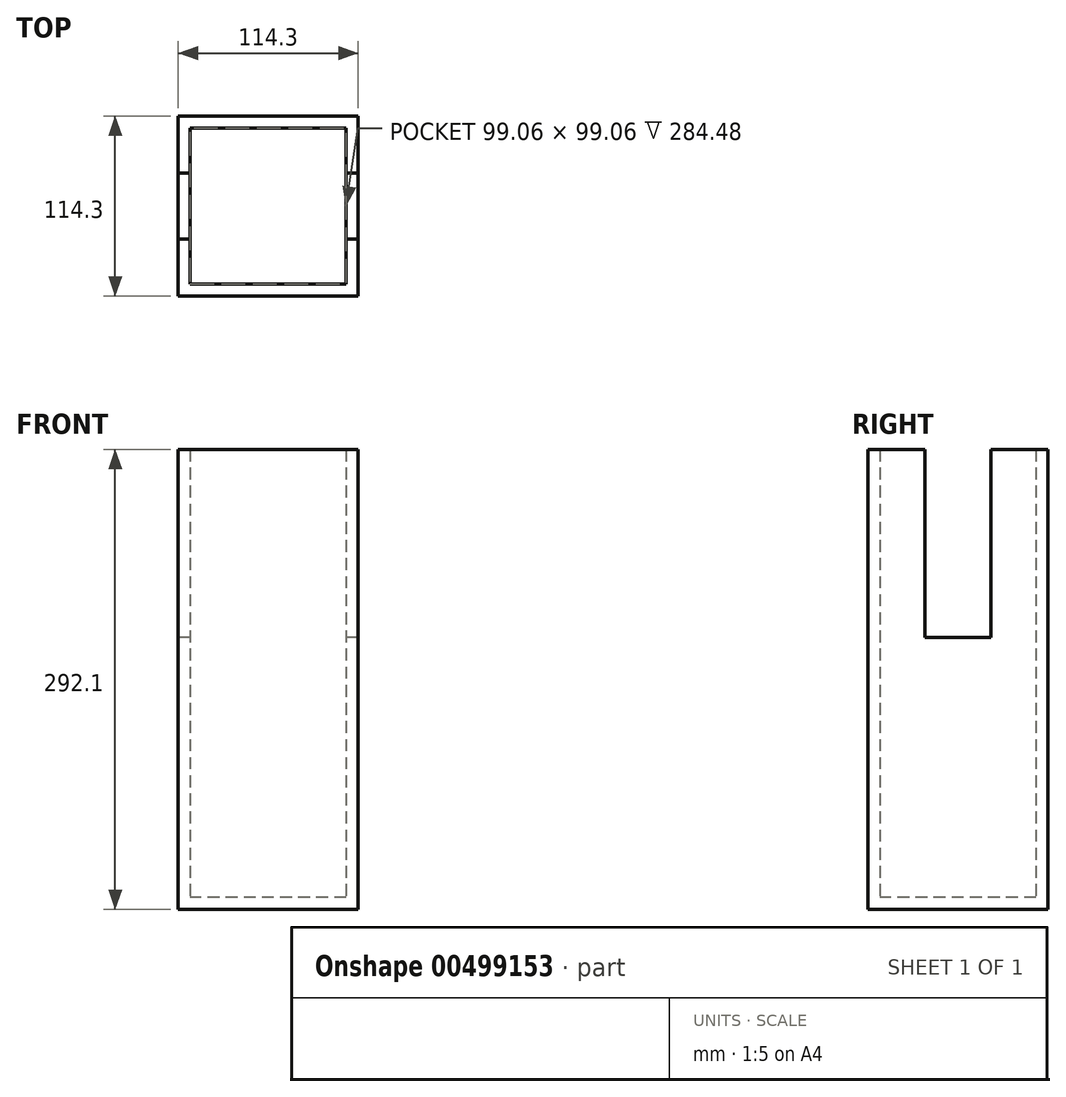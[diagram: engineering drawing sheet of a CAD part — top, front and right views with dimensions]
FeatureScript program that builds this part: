
annotation { "Feature Type Name" : "Feature", "Feature Type Description" : "" }
export const myFeature = defineFeature(function(context is Context, id is Id, definition is map)
    precondition{}
    {
        {
            var Q0;
            Q0=qCreatedBy(makeId("Top.planeOp"),FACE);
            var sketch = newSketch(context, id + "F0", { "sketchPlane" : qUnion([Q0])});
            skLineSegment(sketch, "E0.bottom", {"start": v(57.15, 57.15) * mm, "end": v(-57.15, 57.15) * mm});
            skLineSegment(sketch, "E0.top", {"start": v(57.15, -57.15) * mm, "end": v(-57.15, -57.15) * mm});
            skLineSegment(sketch, "E0.left", {"start": v(57.15, 57.15) * mm, "end": v(57.15, -57.15) * mm});
            skLineSegment(sketch, "E0.right", {"start": v(-57.15, 57.15) * mm, "end": v(-57.15, -57.15) * mm});
            skPoint(sketch, "E0.middle", {"position": v(0, 0) * mm});
            skSolve(sketch);
        }
        {
            var Q0;
            Q0=makeQuery(id+"F0.imprint","IMPRINT",FACE,{"disambiguationData":[TD([[makeQuery(id+"F0.imprint","IMPRINT",EDGE,{"derivedFrom":sQuery(id+"F0.wireOp",EDGE,"E0.bottom")}),1.0]])]});
            extrude(context, id + "F1", {"entities" : qUnion([Q0]), "depth" : 292.1 * mm});
        }
        {
            var Q0;
            Q0=makeQuery(id+"F1.opExtrude","CAP_FACE",FACE,{"disambiguationData":[OSD([sQuery(id+"F0.wireOp",EDGE,"E0.bottom"),sQuery(id+"F0.wireOp",EDGE,"E0.top"),sQuery(id+"F0.wireOp",EDGE,"E0.left"),sQuery(id+"F0.wireOp",EDGE,"E0.right")])],"isStart":false});
            shell(context, id + "F2", {"entities" : qUnion([Q0]), "thickness" : 7.62 * mm});
        }
        {
            var Q0;
            Q0=qCreatedBy(makeId("Right.planeOp"),FACE);
            var sketch = newSketch(context, id + "F3", { "sketchPlane" : qUnion([Q0])});
            skLineSegment(sketch, "E1.bottom", {"start": v(-20.9, 172.81) * mm, "end": v(20.9, 172.81) * mm});
            skLineSegment(sketch, "E1.top", {"start": v(-20.9, 293.4) * mm, "end": v(20.9, 293.4) * mm});
            skLineSegment(sketch, "E1.left", {"start": v(-20.9, 172.81) * mm, "end": v(-20.9, 293.4) * mm});
            skLineSegment(sketch, "E1.right", {"start": v(20.9, 172.81) * mm, "end": v(20.9, 293.4) * mm});
            skPoint(sketch, "E1.middle", {"position": v(0, 233.1) * mm});
            skSolve(sketch);
        }
        {
            var Q0;
            Q0=makeQuery(id+"F3.imprint","IMPRINT",FACE,{"disambiguationData":[TD([[makeQuery(id+"F3.imprint","IMPRINT",EDGE,{"derivedFrom":sQuery(id+"F3.wireOp",EDGE,"E1.bottom")}),1.0]])]});
            extrude(context, id + "F4", {"entities" : qUnion([Q0]), "operationType" : NewBodyOperationType.REMOVE, "endBound" : BoundingType.SYMMETRIC, "depth" : 140.2 * mm});
        }
    });
